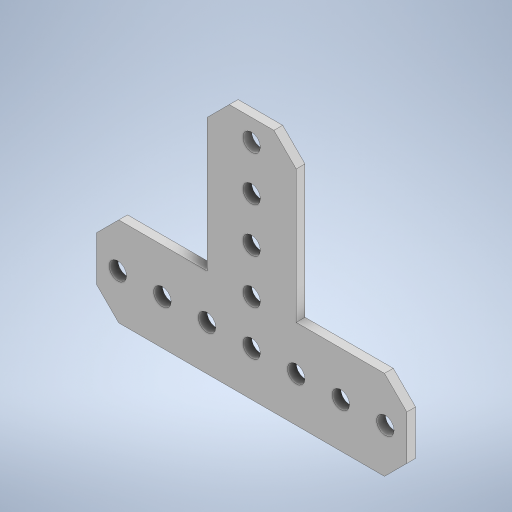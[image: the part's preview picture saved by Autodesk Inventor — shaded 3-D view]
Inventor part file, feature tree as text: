
AUTODESK INVENTOR PART (.ipt)
format: ipt  version: 2024.2 (Build 282272000, 272)  size: 265,216 bytes
history: native  units: in
note: dims shown in document units (in); Inventor stores cm internally (conversion verified against a paired STEP export)
features: chamfer x1
ambient origin geometry x8: Origin, YZ Plane, XZ Plane, XY Plane, X Axis, Y Axis, Z Axis, Center Point
bodies: Solid1 (feature_tree)
feature tree (1):
  chamfer  "Chamfer1"  [1 undecoded]
note: 1 required parameter value undecoded (feature->parameter linkage not recoverable at this tier; creation-order binding heuristic only, values carry confidence <= 0.55)
